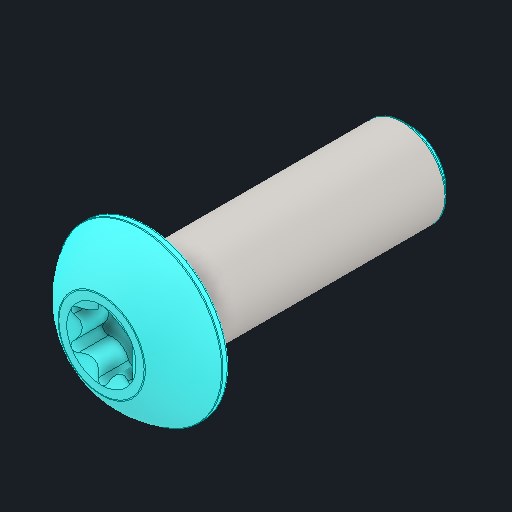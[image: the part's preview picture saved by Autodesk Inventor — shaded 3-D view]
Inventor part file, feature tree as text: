
AUTODESK INVENTOR PART (.ipt)
format: ipt  version: 2025 (Build 290162000, 162)  size: 180,224 bytes
history: native  units: in
note: dims shown in document units (in); Inventor stores cm internally (conversion verified against a paired STEP export)
features: fillet x1
ambient origin geometry x8: Origin, YZ Plane, XZ Plane, XY Plane, X Axis, Y Axis, Z Axis, Center Point
bodies: Solid1 (feature_tree)
feature tree (1):
  fillet  "Fillet1"  [1 undecoded]
note: 1 required parameter value undecoded (feature->parameter linkage not recoverable at this tier; creation-order binding heuristic only, values carry confidence <= 0.55)
